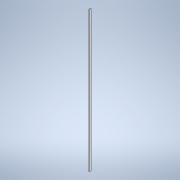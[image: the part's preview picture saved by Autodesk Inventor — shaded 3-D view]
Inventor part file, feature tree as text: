
AUTODESK INVENTOR PART (.ipt)
format: ipt  version: 2021 (Build 250183000, 183)  size: 93,696 bytes
history: native  units: mm
features: extrude x1, sketch x1
ambient origin geometry x8: Origin, YZ Plane, XZ Plane, XY Plane, X Axis, Y Axis, Z Axis, Center Point
bodies: Solid1 (feature_tree)
feature tree (2):
  extrude  "Extrusion1"  Depth=20.0mm
  sketch  "Sketch1"  dims[d0=10.0mm d1=20.0mm d2=1785.5mm d3=0.0mm]
